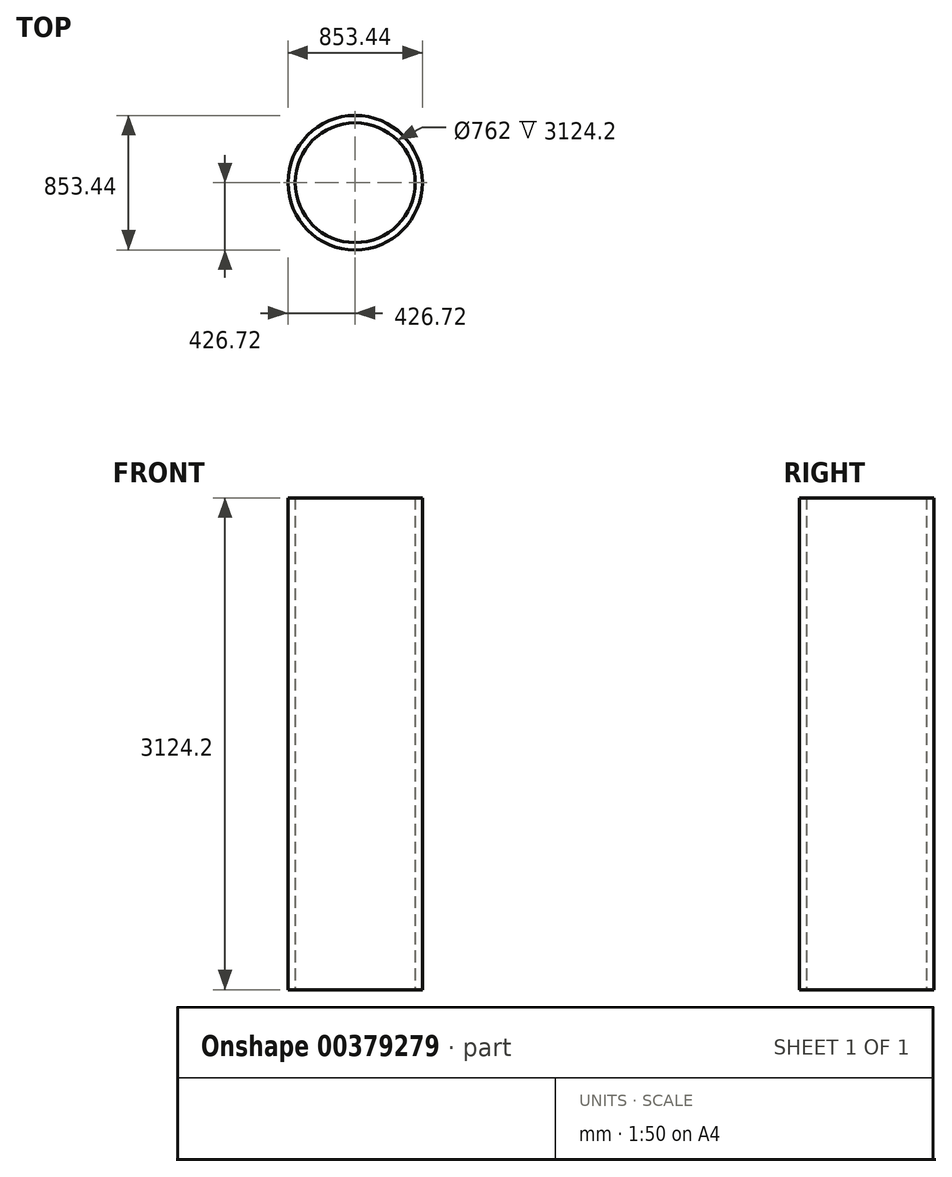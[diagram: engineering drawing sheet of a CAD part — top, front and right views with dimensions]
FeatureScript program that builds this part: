
annotation { "Feature Type Name" : "Feature", "Feature Type Description" : "" }
export const myFeature = defineFeature(function(context is Context, id is Id, definition is map)
    precondition{}
    {
        {
            var Q0;
            Q0=qCreatedBy(makeId("Top.planeOp"),FACE);
            var sketch = newSketch(context, id + "F0", { "sketchPlane" : qUnion([Q0])});
            skCircle(sketch, "E0", {"center": v(0, 0) * mm, "radius": 381 * mm});
            skCircle(sketch, "E1.0", {"center": v(0, 0) * mm, "radius": 426.72 * mm});
            skSolve(sketch);
        }
        {
            var Q0;
            Q0=makeQuery(id+"F0.imprint","IMPRINT",FACE,{"disambiguationData":[TD([[makeQuery(id+"F0.imprint","IMPRINT",EDGE,{"derivedFrom":sQuery(id+"F0.wireOp",EDGE,"E0")}),-1.0]])]});
            extrude(context, id + "F1", {"entities" : qUnion([Q0]), "depth" : 1803.4 * mm, "hasSecondDirection" : true, "secondDirectionOppositeDirection" : true, "secondDirectionDepth" : 1320.8 * mm});
        }
    });
